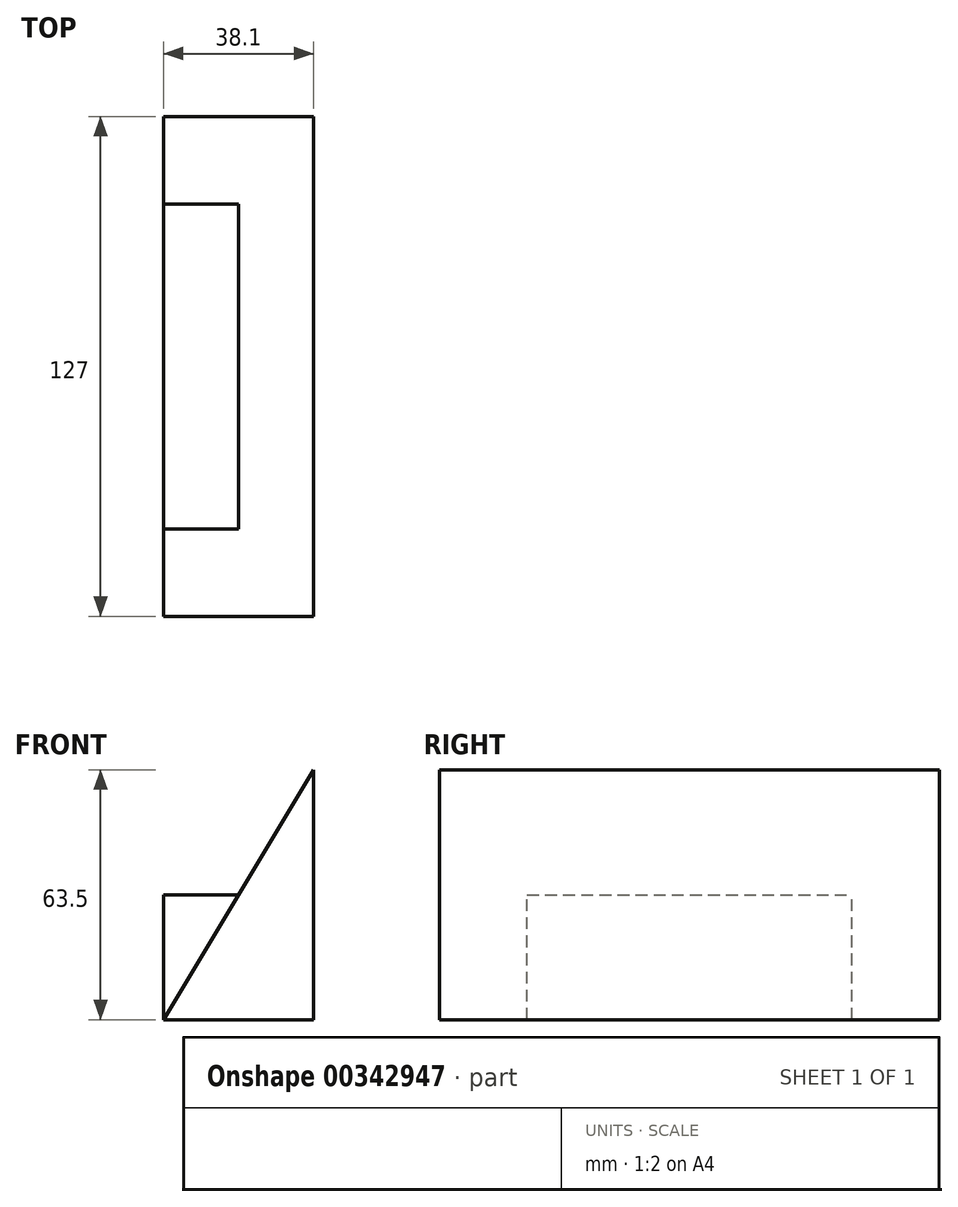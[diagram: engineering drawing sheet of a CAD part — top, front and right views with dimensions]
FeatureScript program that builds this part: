
annotation { "Feature Type Name" : "Feature", "Feature Type Description" : "" }
export const myFeature = defineFeature(function(context is Context, id is Id, definition is map)
    precondition{}
    {
        {
            var Q0;
            Q0=qCreatedBy(makeId("Front.planeOp"),FACE);
            var sketch = newSketch(context, id + "F0", { "sketchPlane" : qUnion([Q0])});
            skLineSegment(sketch, "E0", {"start": v(-19.05, -24.05) * mm, "end": v(19.05, -24.05) * mm});
            skLineSegment(sketch, "E1", {"start": v(19.05, -24.05) * mm, "end": v(19.05, 39.45) * mm});
            skLineSegment(sketch, "E2", {"start": v(-19.05, -24.05) * mm, "end": v(19.05, 39.45) * mm});
            skLineSegment(sketch, "E3", {"start": v(-19.05, -24.05) * mm, "end": v(-19.05, 7.7) * mm});
            skLineSegment(sketch, "E4", {"start": v(-19.05, 7.7) * mm, "end": v(0, 7.7) * mm});
            skSolve(sketch);
        }
        {
            var Q0;
            {var subQ0=sQuery(id+"F0.wireOp",EDGE,"E0");Q0=makeQuery(id+"F0.imprint","IMPRINT",FACE,{"disambiguationData":[TD([[makeQuery(id+"F0.imprint","IMPRINT",EDGE,{"derivedFrom":subQ0}),1.0]])]});}
            extrude(context, id + "F1", {"entities" : qUnion([Q0]), "depth" : 63.5 * mm});
        }
        {
            var Q0;
            Q0=makeQuery(id+"F1.opExtrude","CAP_FACE",FACE,{"disambiguationData":[OSD([sQuery(id+"F0.wireOp",EDGE,"E0"),sQuery(id+"F0.wireOp",EDGE,"E1"),sQuery(id+"F0.wireOp",EDGE,"E2")])],"isStart":true});
            extrude(context, id + "F2", {"entities" : qUnion([Q0]), "operationType" : NewBodyOperationType.ADD, "depth" : 63.5 * mm});
        }
        {
            var Q0;
            {var subQ0=sQuery(id+"F0.wireOp",EDGE,"E3");Q0=makeQuery(id+"F0.imprint","IMPRINT",FACE,{"disambiguationData":[TD([[makeQuery(id+"F0.imprint","IMPRINT",EDGE,{"derivedFrom":subQ0}),-1.0]])]});}
            extrude(context, id + "F3", {"entities" : qUnion([Q0]), "operationType" : NewBodyOperationType.ADD, "depth" : 41.27 * mm});
        }
        {
            var Q0;
            Q0=makeQuery(id+"F3.opExtrude","CAP_FACE",FACE,{"disambiguationData":[OSD([sQuery(id+"F0.wireOp",EDGE,"E2"),sQuery(id+"F0.wireOp",EDGE,"E3"),sQuery(id+"F0.wireOp",EDGE,"E4")])],"isStart":true});
            extrude(context, id + "F4", {"entities" : qUnion([Q0]), "operationType" : NewBodyOperationType.ADD, "depth" : 41.27 * mm});
        }
    });
